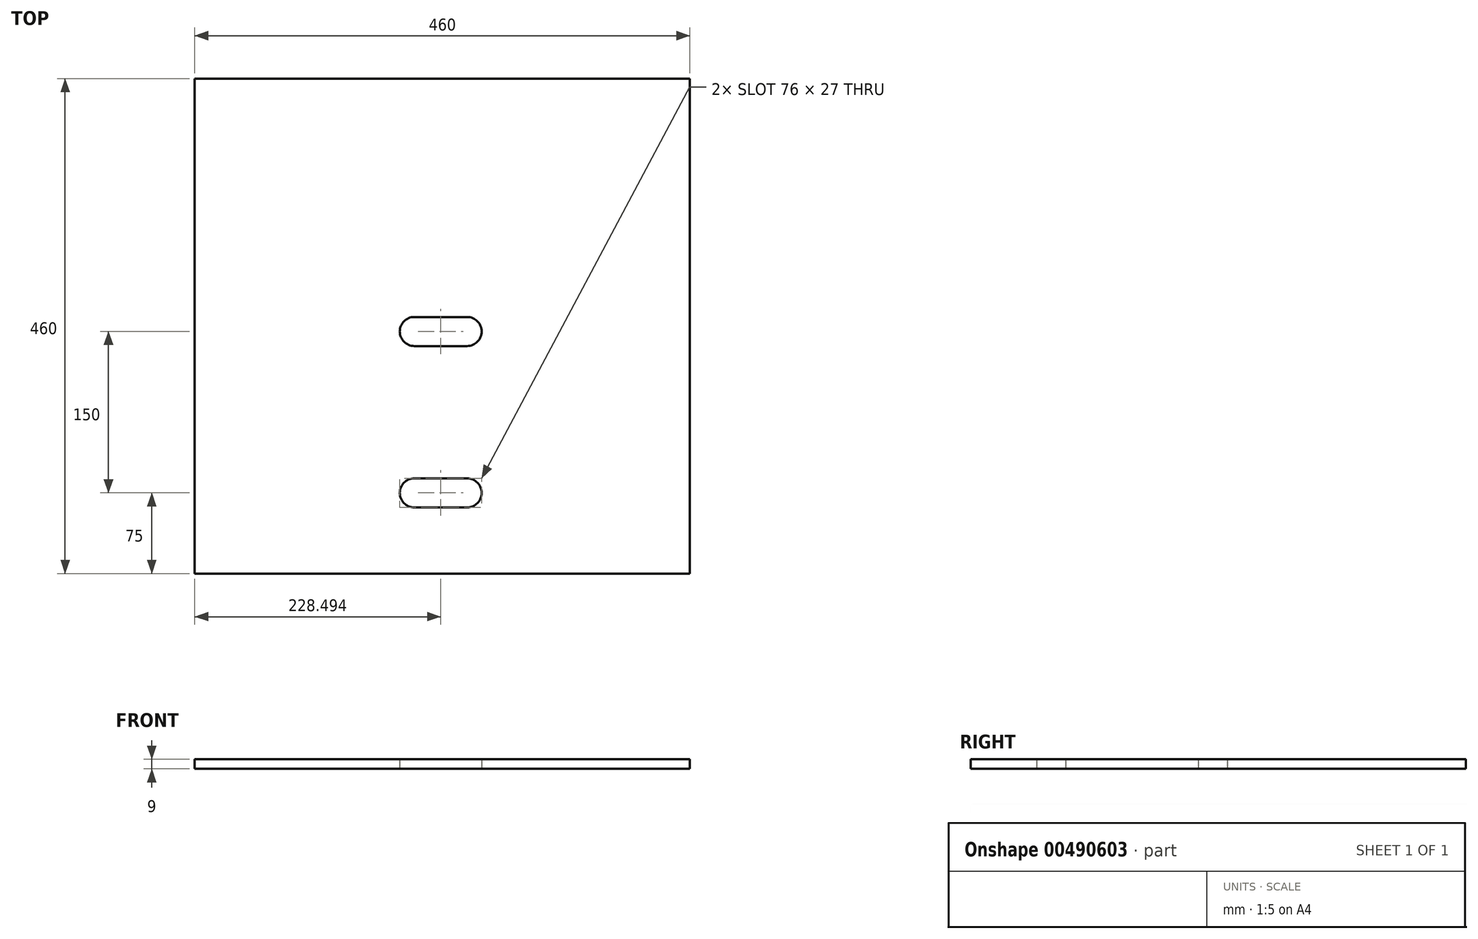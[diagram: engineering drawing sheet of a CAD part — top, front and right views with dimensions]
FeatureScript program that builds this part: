
annotation { "Feature Type Name" : "Feature", "Feature Type Description" : "" }
export const myFeature = defineFeature(function(context is Context, id is Id, definition is map)
    precondition{}
    {
        {
            var Q0;
            Q0=qCreatedBy(makeId("Top.planeOp"),FACE);
            var sketch = newSketch(context, id + "F0", { "sketchPlane" : qUnion([Q0]), "disableImprinting" : false});
            skLineSegment(sketch, "E0.bottom", {"start": v(0, 0) * mm, "end": v(460, 0) * mm});
            skLineSegment(sketch, "E0.top", {"start": v(0, 460) * mm, "end": v(460, 460) * mm});
            skLineSegment(sketch, "E0.left", {"start": v(0, 0) * mm, "end": v(0, 460) * mm});
            skLineSegment(sketch, "E0.right", {"start": v(460, 0) * mm, "end": v(460, 460) * mm});
            skLineSegment(sketch, "E1", {"start": v(100.83, 75) * mm, "end": v(362.57, 75) * mm, "construction": true});
            skLineSegment(sketch, "E2", {"start": v(362.57, 225) * mm, "end": v(100.83, 225) * mm, "construction": true});
            skLineSegment(sketch, "E3", {"start": v(230, 0) * mm, "end": v(230, 281.63) * mm, "construction": true});
            skLineSegment(sketch, "E4.0", {"start": v(253, 211.5) * mm, "end": v(204, 211.5) * mm});
            skLineSegment(sketch, "E5.0", {"start": v(204, 61.5) * mm, "end": v(253, 61.5) * mm});
            skLineSegment(sketch, "E6", {"start": v(204, 238.5) * mm, "end": v(253, 238.5) * mm});
            skLineSegment(sketch, "E7", {"start": v(253, 88.5) * mm, "end": v(204, 88.5) * mm});
            skArc(sketch, "E8", {"start": v(253, 211.5) * mm, "mid": v(266.5, 225) * mm, "end": v(253, 238.5) * mm});
            skArc(sketch, "E9", {"start": v(204, 238.5) * mm, "mid": v(190.5, 225) * mm, "end": v(204, 211.5) * mm});
            skArc(sketch, "E10", {"start": v(204, 88.5) * mm, "mid": v(190.5, 75) * mm, "end": v(204, 61.5) * mm});
            skArc(sketch, "E11", {"start": v(253, 61.5) * mm, "mid": v(266.5, 75) * mm, "end": v(253, 88.5) * mm});
            skSolve(sketch);
        }
        {
            var Q0;
            Q0 = qSketchRegion(id + "F0", true);
            extrude(context, id + "F1", {"entities" : qUnion([Q0]), "depth" : 9 * mm});
        }
    });
